# Revit family: Walls_Moving_walls_Komandor_MAW_48_without_door_Z1
name_source: partatom
category: Generic Models
revit_build: Autodesk Revit 2014 (Build: 20130308_1515(x64)
units: mm (PartAtom-declared; Revit-internal decimal feet)

## types (1)
- Walls_Moving_walls_Komandor_MAW_48_without_door_Z1
    BIMobject category = Folding & Moving Walls
    COBIe Type Category = Wall MOVABLE
    Date of publishing = 12/1/2016
    Design country = Poland
    Edition number = 1
    Glass Panel 10 mm = Yes
    IFC Classification = Wall
    Installation instructions = http://www.komandorwalls.com
    Manufacturer country = Poland
    Manufacturer name = Komandor
    Masterformat 2014 Code = 07 42 00
    Masterformat 2014 Description = Wall Panels
    Material main = Aluminium
    Material secondary = Glass
    NBS Reference Code = 25-30-20-80
    NBS Reference Description = Sliding Stacking Panel Partition Systems
    Nominal height = 0
    Nominal width = 0
    OmniClass Code = 23-15 13 19
    OmniClass Description = Wall Panels
    Panel Material = Glass
    Product Guid = ab983b70-f0a7-47e8-bc3c-1314107ca74d
    Product SKU = maw48
    Product data url = https://bimobject.com
    Product family = Walls
    Product group = MAW
    Profile Material = Komandor_Aluminum
    QR code = http://bimobject.com
    UNSPSC Code = 301615
    Uniclass 1.4 Code = L83122
    Uniclass 1.4 Description = Wall units
    Uniclass 2.0 Code = SS-25-30-20-80
    Uniclass 2.0 Description = Sliding Stacking Panel Partition Systems
    Uniclass 2015 Code = EF_25
    Uniclass 2015 Name = Wall and barrier elements
    Uniformat II Code = C3010
    Uniformat II Description = Wall Finishes
    Weight Net (Kg) = 0
    Youtube clip = https://www.youtube.com

## geometry (parser evidence)
native form markers: Sweep x11
no freeform markers — native parametric forms only
